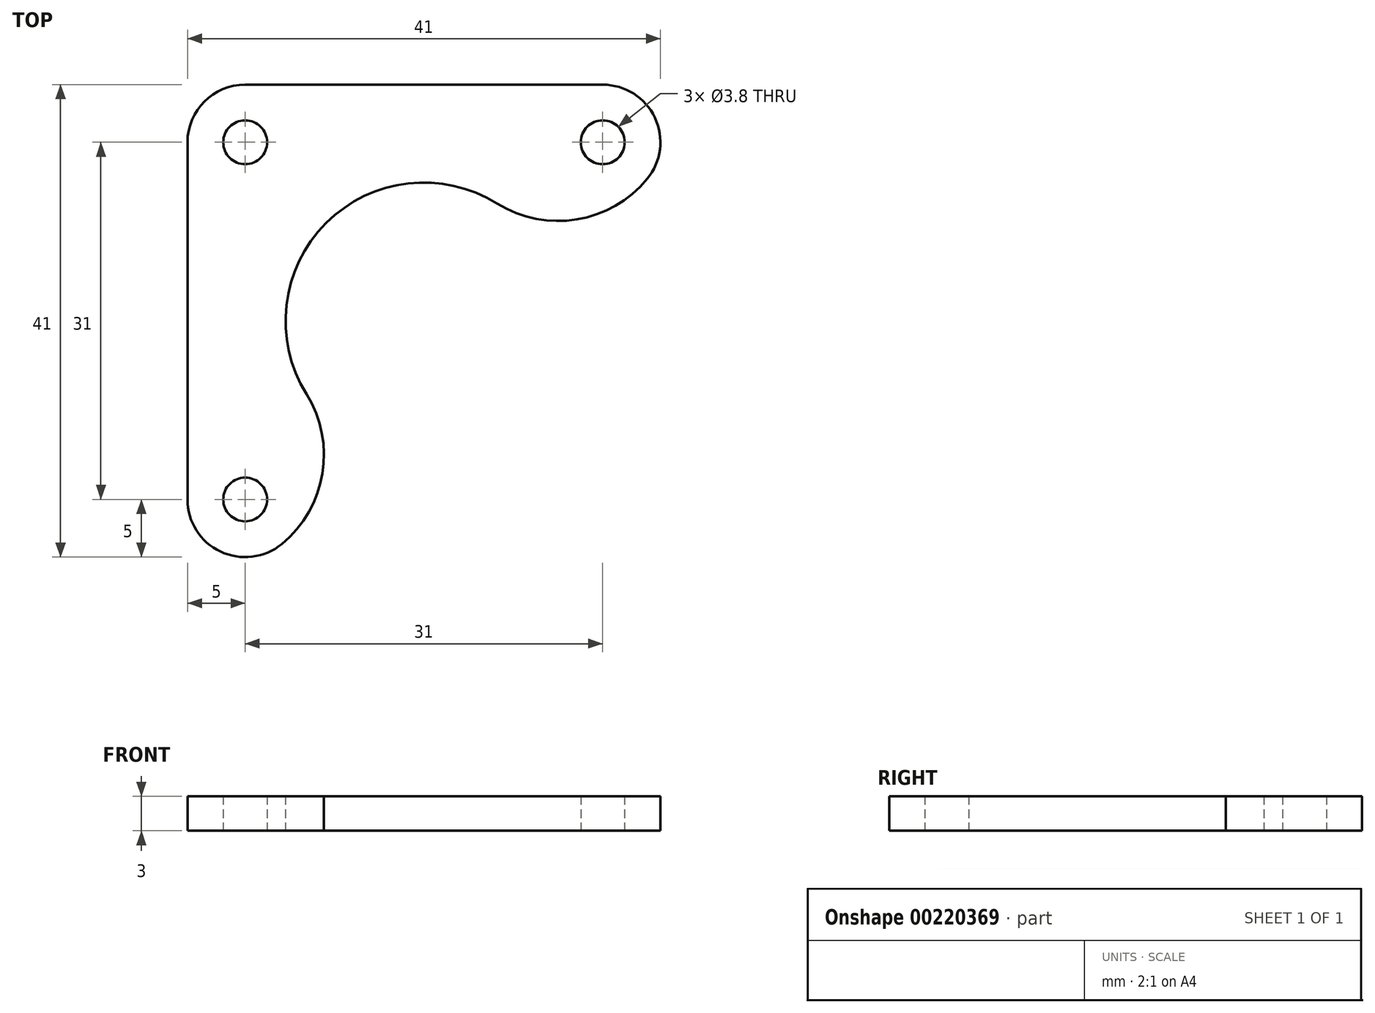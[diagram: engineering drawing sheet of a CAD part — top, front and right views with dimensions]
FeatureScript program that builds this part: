
annotation { "Feature Type Name" : "Feature", "Feature Type Description" : "" }
export const myFeature = defineFeature(function(context is Context, id is Id, definition is map)
    precondition{}
    {
        {
            var Q0;
            Q0=qCreatedBy(makeId("Top.planeOp"),FACE);
            var sketch = newSketch(context, id + "F0", { "sketchPlane" : qUnion([Q0])});
            skLineSegment(sketch, "E0.bottom", {"start": v(15.5, -15.5) * mm, "end": v(-15.5, -15.5) * mm, "construction": true});
            skLineSegment(sketch, "E0.top", {"start": v(15.5, 15.5) * mm, "end": v(-15.5, 15.5) * mm, "construction": true});
            skLineSegment(sketch, "E0.left", {"start": v(15.5, -15.5) * mm, "end": v(15.5, 15.5) * mm, "construction": true});
            skLineSegment(sketch, "E0.right", {"start": v(-15.5, -15.5) * mm, "end": v(-15.5, 15.5) * mm, "construction": true});
            skPoint(sketch, "E0.middle", {"position": v(0, 0) * mm});
            skCircle(sketch, "E1", {"center": v(-15.5, 15.5) * mm, "radius": 1.9 * mm});
            skCircle(sketch, "E2", {"center": v(15.5, 15.5) * mm, "radius": 1.9 * mm});
            skCircle(sketch, "E3", {"center": v(-15.5, -15.5) * mm, "radius": 1.9 * mm});
            skLineSegment(sketch, "E4.bottom", {"start": v(-21, 21) * mm, "end": v(21, 21) * mm, "construction": true});
            skLineSegment(sketch, "E4.top", {"start": v(-21, -21) * mm, "end": v(21, -21) * mm, "construction": true});
            skLineSegment(sketch, "E4.left", {"start": v(-21, 21) * mm, "end": v(-21, -21) * mm, "construction": true});
            skLineSegment(sketch, "E4.right", {"start": v(21, 21) * mm, "end": v(21, -21) * mm, "construction": true});
            skCircle(sketch, "E5", {"center": v(15.5, 15.5) * mm, "radius": 5 * mm});
            skCircle(sketch, "E6", {"center": v(-15.5, 15.5) * mm, "radius": 5 * mm});
            skCircle(sketch, "E7", {"center": v(-15.5, -15.5) * mm, "radius": 5 * mm});
            skLineSegment(sketch, "E8", {"start": v(-15.5, 20.5) * mm, "end": v(15.5, 20.5) * mm});
            skLineSegment(sketch, "E9", {"start": v(-20.5, 15.5) * mm, "end": v(-20.5, -15.5) * mm});
            skArc(sketch, "E10", {"start": v(-10.18, -6.35) * mm, "mid": v(-8.49, 8.49) * mm, "end": v(6.35, 10.18) * mm});
            skArc(sketch, "E11", {"start": v(6.35, 10.18) * mm, "mid": v(13.26, 8.8) * mm, "end": v(19.37, 12.33) * mm});
            skArc(sketch, "E12", {"start": v(-12.33, -19.37) * mm, "mid": v(-8.8, -13.26) * mm, "end": v(-10.18, -6.35) * mm});
            skSolve(sketch);
        }
        {
            var Q0;
            Q0=makeQuery(id+"F0.imprint","IMPRINT",FACE,{"disambiguationData":[TD([[makeQuery(id+"F0.imprint","IMPRINT",EDGE,{"derivedFrom":sQuery(id+"F0.wireOp",EDGE,"E1")}),-1.0]])]});
            var Q1;
            {var subQ0=sQuery(id+"F0.wireOp",EDGE,"E8");Q1=makeQuery(id+"F0.imprint","IMPRINT",FACE,{"disambiguationData":[TD([[makeQuery(id+"F0.imprint","IMPRINT",EDGE,{"derivedFrom":subQ0}),-1.0]])]});}
            var Q2;
            Q2=makeQuery(id+"F0.imprint","IMPRINT",FACE,{"disambiguationData":[TD([[makeQuery(id+"F0.imprint","IMPRINT",EDGE,{"derivedFrom":sQuery(id+"F0.wireOp",EDGE,"E2")}),-1.0]])]});
            var Q3;
            Q3=makeQuery(id+"F0.imprint","IMPRINT",FACE,{"disambiguationData":[TD([[makeQuery(id+"F0.imprint","IMPRINT",EDGE,{"derivedFrom":sQuery(id+"F0.wireOp",EDGE,"E3")}),-1.0]])]});
            extrude(context, id + "F1", {"entities" : qUnion([Q0, Q1, Q2, Q3]), "depth" : 3 * mm});
        }
    });
